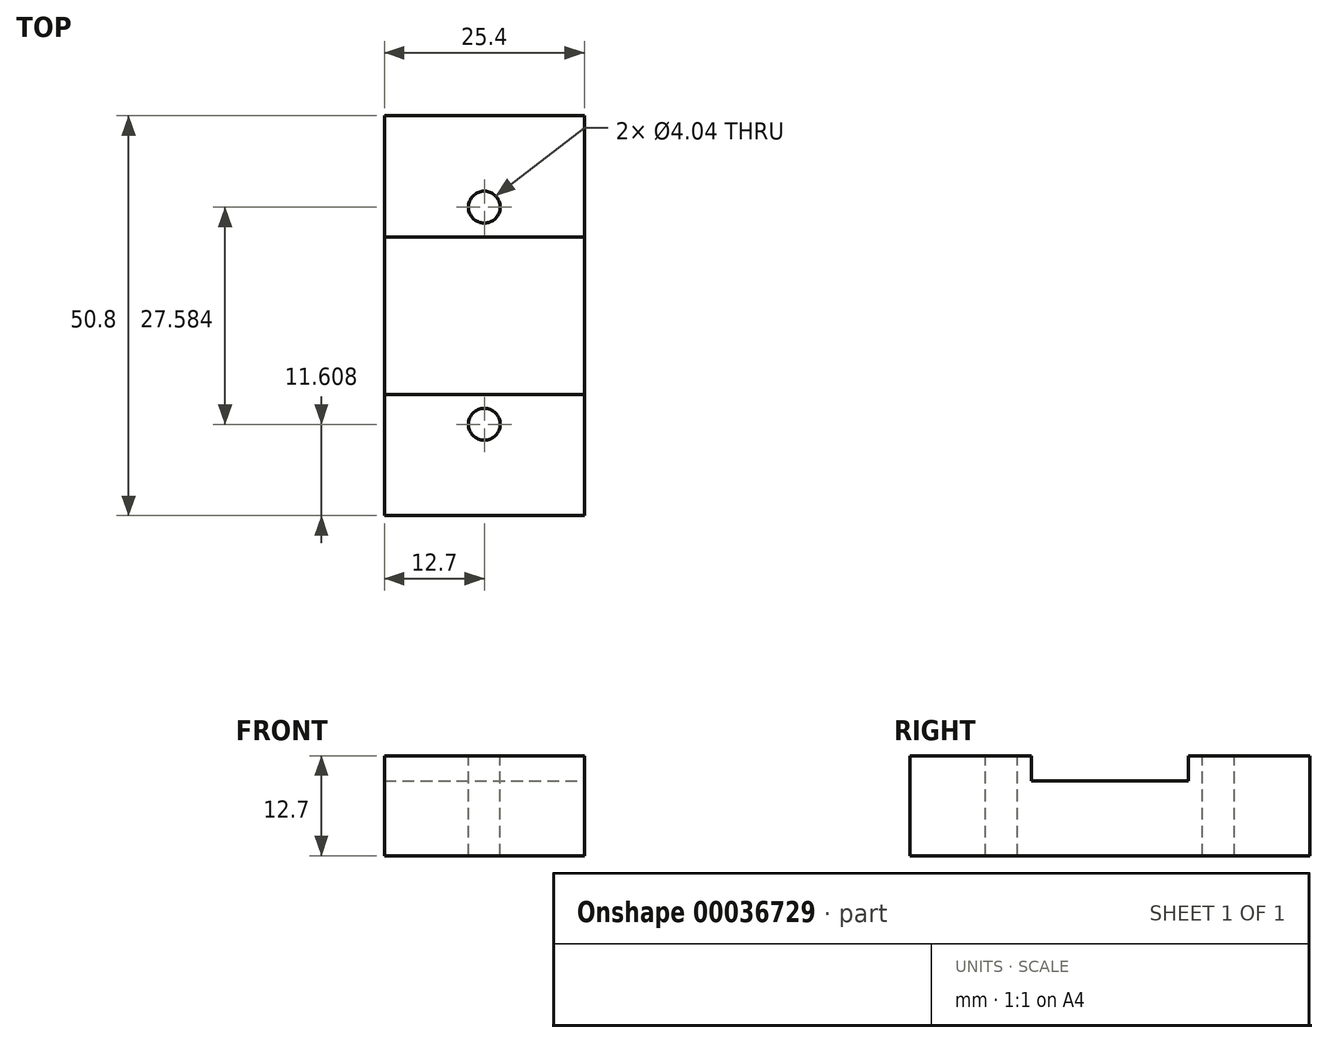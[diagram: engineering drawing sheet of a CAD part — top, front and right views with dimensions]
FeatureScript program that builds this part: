
annotation { "Feature Type Name" : "Feature", "Feature Type Description" : "" }
export const myFeature = defineFeature(function(context is Context, id is Id, definition is map)
    precondition{}
    {
        {
            var Q0;
            Q0=qCreatedBy(makeId("Top.planeOp"),FACE);
            var sketch = newSketch(context, id + "F0", { "sketchPlane" : qUnion([Q0])});
            skLineSegment(sketch, "E0.bottom", {"start": v(12.7, 25.4) * mm, "end": v(-12.7, 25.4) * mm});
            skLineSegment(sketch, "E0.top", {"start": v(12.7, -25.4) * mm, "end": v(-12.7, -25.4) * mm});
            skLineSegment(sketch, "E0.left", {"start": v(12.7, 25.4) * mm, "end": v(12.7, -25.4) * mm});
            skLineSegment(sketch, "E0.right", {"start": v(-12.7, 25.4) * mm, "end": v(-12.7, -25.4) * mm});
            skPoint(sketch, "E0.middle", {"position": v(0, 0) * mm});
            skSolve(sketch);
        }
        {
            var Q0;
            Q0 = qSketchRegion(id + "F0", true);
            extrude(context, id + "F1", {"entities" : qUnion([Q0]), "depth" : 12.7 * mm});
        }
        {
            var Q0;
            Q0=makeQuery(id+"F1.opExtrude","CAP_FACE",FACE,{"disambiguationData":[OSD([sQuery(id+"F0.wireOp",EDGE,"E0.bottom"),sQuery(id+"F0.wireOp",EDGE,"E0.top"),sQuery(id+"F0.wireOp",EDGE,"E0.left"),sQuery(id+"F0.wireOp",EDGE,"E0.right")])],"isStart":false});
            var sketch = newSketch(context, id + "F2", { "sketchPlane" : qUnion([Q0])});
            skLineSegment(sketch, "E1.bottom", {"start": v(-12.7, 9.98) * mm, "end": v(12.7, 9.98) * mm});
            skLineSegment(sketch, "E1.top", {"start": v(-12.7, -9.98) * mm, "end": v(12.7, -9.98) * mm});
            skLineSegment(sketch, "E1.left", {"start": v(-12.7, 9.98) * mm, "end": v(-12.7, -9.98) * mm});
            skLineSegment(sketch, "E1.right", {"start": v(12.7, 9.98) * mm, "end": v(12.7, -9.98) * mm});
            skLineSegment(sketch, "E2", {"start": v(-12.7, 0) * mm, "end": v(12.7, 0) * mm, "construction": true});
            skSolve(sketch);
        }
        {
            var Q0;
            Q0 = qSketchRegion(id + "F2", true);
            extrude(context, id + "F3", {"entities" : qUnion([Q0]), "operationType" : NewBodyOperationType.REMOVE, "oppositeDirection" : true, "depth" : 3.17 * mm});
        }
        {
            var Q0;
            {var subQ0=sQuery(id+"F0.wireOp",EDGE,"E0.bottom");var subQ1=sQuery(id+"F0.wireOp",EDGE,"E0.right");var subQ2=sQuery(id+"F0.wireOp",EDGE,"E0.left");Q0=makeQuery(id+"F3.boolean.opBoolean","SPLIT",FACE,{"disambiguationData":[TD([makeQuery(id+"F1.opExtrude","SWEPT_FACE",FACE,{"disambiguationData":[OSD([subQ0])]})])],"derivedFrom":makeQuery(id+"F1.opExtrude","CAP_FACE",FACE,{"disambiguationData":[OSD([subQ0,sQuery(id+"F0.wireOp",EDGE,"E0.top"),subQ2,subQ1])],"isStart":false})});}
            var sketch = newSketch(context, id + "F4", { "sketchPlane" : qUnion([Q0])});
            skPoint(sketch, "E3", {"position": v(0, 13.8) * mm});
            skPoint(sketch, "E3.positionSnap0", {"position": v(-12.7, 13.8) * mm});
            skPoint(sketch, "E3.positionSnap1", {"position": v(0, 25.4) * mm});
            skPoint(sketch, "E4", {"position": v(0, -13.8) * mm});
            skSolve(sketch);
        }
        {
            var Q0;
            Q0=sQuery(id+"F4.wireOp",VERTEX,"E3");
            var Q1;
            Q1=sQuery(id+"F4.wireOp",VERTEX,"E4");
            var Q2;
            Q2=makeQuery(id+"F1.opExtrude","SWEPT_BODY",BODY,{"disambiguationData":[OSD([sQuery(id+"F0.wireOp",EDGE,"E0.bottom"),sQuery(id+"F0.wireOp",EDGE,"E0.top"),sQuery(id+"F0.wireOp",EDGE,"E0.left"),sQuery(id+"F0.wireOp",EDGE,"E0.right")])]});
            hole(context, id + "F5", {"style" : HoleStyle.SIMPLE, "endStyle" : HoleEndStyle.THROUGH, "standardTappedOrClearance" : lookupTablePath({ "standard" : "ANSI", "engagement" : "75%", "pitch" : "32 tpi", "size" : "#10", "type" : "Tapped" }), "standardBlindInLast" : lookupTablePath({ "standard" : "ANSI", "engagement" : "75%", "pitch" : "32 tpi", "size" : "#10", "type" : "Tapped" }), "holeDiameter" : 4.04 * mm, "showTappedDepth" : true, "tappedDepth" : 6.35 * mm, "tapClearance" : 3, "locations" : qUnion([Q0, Q1]), "scope" : qUnion([Q2]), "majorDiameter" : 4.83 * mm});
        }
    });
